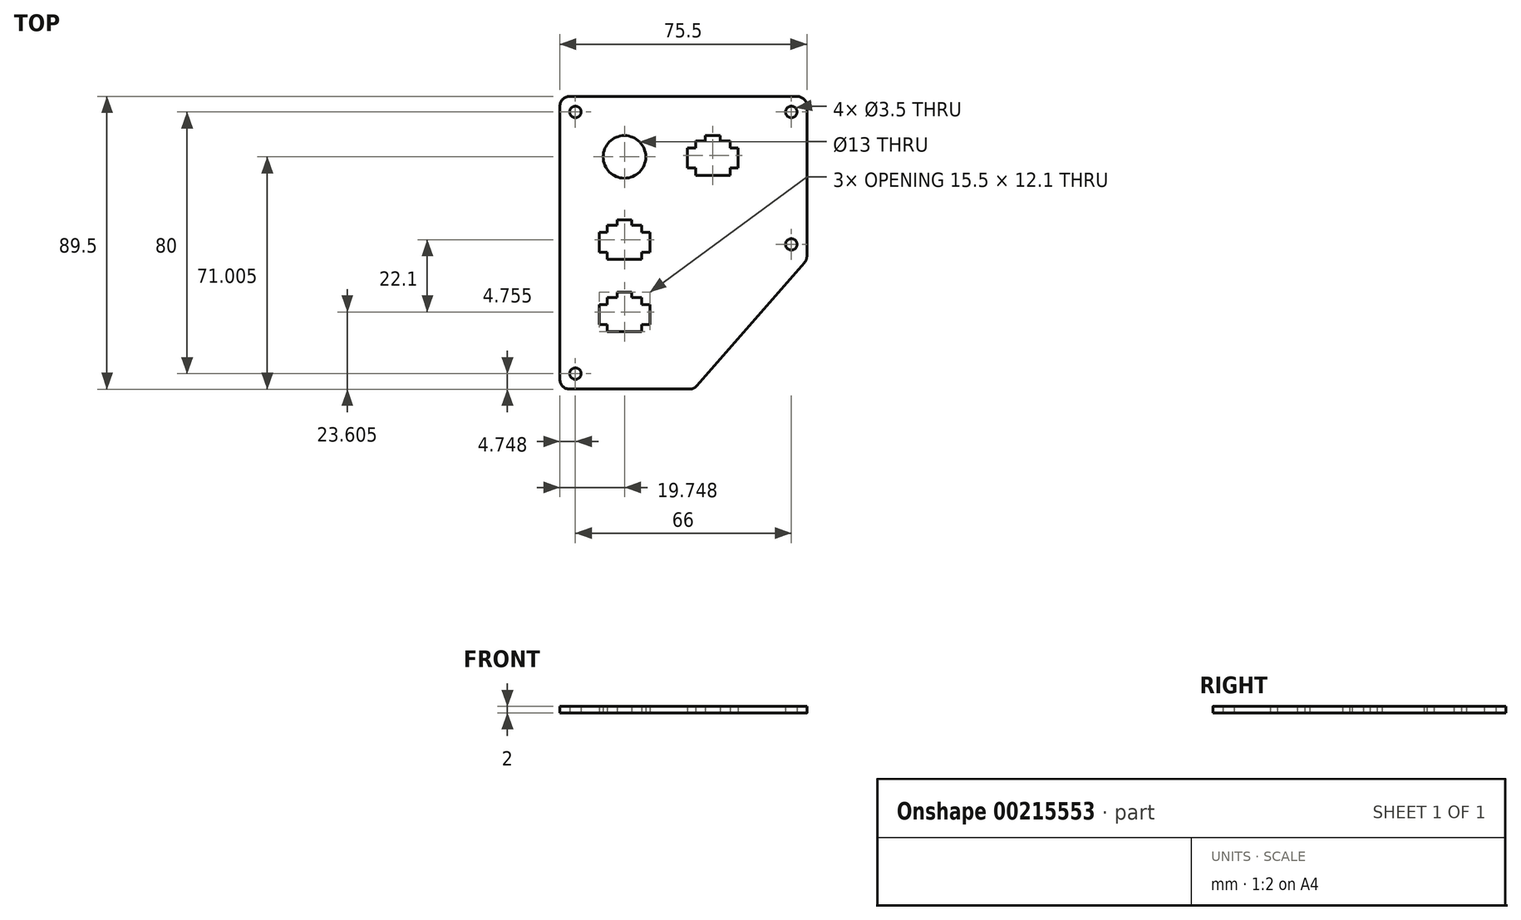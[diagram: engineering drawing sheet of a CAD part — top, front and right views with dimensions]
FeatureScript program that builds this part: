
annotation { "Feature Type Name" : "Feature", "Feature Type Description" : "" }
export const myFeature = defineFeature(function(context is Context, id is Id, definition is map)
    precondition{}
    {
        {
            var Q0;
            Q0=qCreatedBy(makeId("Top.planeOp"),FACE);
            var sketch = newSketch(context, id + "F0", { "sketchPlane" : qUnion([Q0])});
            skLineSegment(sketch, "E0", {"start": v(-37.21, 48.66) * mm, "end": v(38.29, 48.66) * mm});
            skLineSegment(sketch, "E1", {"start": v(38.29, 48.66) * mm, "end": v(38.29, -1.34) * mm});
            skLineSegment(sketch, "E2", {"start": v(38.29, -1.34) * mm, "end": v(3.79, -40.84) * mm});
            skLineSegment(sketch, "E3", {"start": v(3.79, -40.84) * mm, "end": v(-37.21, -40.84) * mm});
            skLineSegment(sketch, "E4", {"start": v(-37.21, -40.84) * mm, "end": v(-37.21, 48.66) * mm});
            skCircle(sketch, "E5", {"center": v(-32.46, 43.91) * mm, "radius": 1.75 * mm});
            skCircle(sketch, "E6", {"center": v(33.54, 43.91) * mm, "radius": 1.75 * mm});
            skCircle(sketch, "E7", {"center": v(33.54, 3.41) * mm, "radius": 1.75 * mm});
            skCircle(sketch, "E8", {"center": v(-32.46, -36.09) * mm, "radius": 1.75 * mm});
            skLineSegment(sketch, "E9", {"start": v(-25.21, 36.66) * mm, "end": v(26.29, 36.66) * mm, "construction": true});
            skLineSegment(sketch, "E10", {"start": v(26.29, 36.66) * mm, "end": v(26.29, -2.68) * mm, "construction": true});
            skLineSegment(sketch, "E11", {"start": v(26.29, -2.68) * mm, "end": v(2.25, -28.84) * mm, "construction": true});
            skLineSegment(sketch, "E12", {"start": v(2.25, -28.84) * mm, "end": v(-25.21, -28.84) * mm, "construction": true});
            skLineSegment(sketch, "E13", {"start": v(-25.21, -28.84) * mm, "end": v(-25.21, 36.66) * mm, "construction": true});
            skSolve(sketch);
        }
        {
            var Q0;
            Q0=qCreatedBy(makeId("Top.planeOp"),FACE);
            var sketch = newSketch(context, id + "F1", { "sketchPlane" : qUnion([Q0])});
            skLineSegment(sketch, "E14.bottom", {"start": v(-12.21, 9.31) * mm, "end": v(-22.71, 9.31) * mm});
            skLineSegment(sketch, "E14.top", {"start": v(-12.21, -1.19) * mm, "end": v(-22.71, -1.19) * mm});
            skLineSegment(sketch, "E14.left", {"start": v(-12.21, 9.31) * mm, "end": v(-12.21, -1.19) * mm});
            skLineSegment(sketch, "E14.right", {"start": v(-22.71, 9.31) * mm, "end": v(-22.71, -1.19) * mm});
            skPoint(sketch, "E14.middle", {"position": v(-17.46, 4.06) * mm});
            skLineSegment(sketch, "E15.bottom", {"start": v(-12.21, 7.11) * mm, "end": v(-9.71, 7.11) * mm});
            skLineSegment(sketch, "E15.top", {"start": v(-12.21, 1.01) * mm, "end": v(-9.71, 1.01) * mm});
            skLineSegment(sketch, "E15.left", {"start": v(-12.21, 7.11) * mm, "end": v(-12.21, 1.01) * mm});
            skLineSegment(sketch, "E15.right", {"start": v(-9.71, 7.11) * mm, "end": v(-9.71, 1.01) * mm});
            skPoint(sketch, "E15.middle", {"position": v(-10.96, 4.06) * mm});
            skLineSegment(sketch, "E16.bottom", {"start": v(-22.71, 7.11) * mm, "end": v(-25.21, 7.11) * mm});
            skLineSegment(sketch, "E16.top", {"start": v(-22.71, 1.01) * mm, "end": v(-25.21, 1.01) * mm});
            skLineSegment(sketch, "E16.left", {"start": v(-22.71, 7.11) * mm, "end": v(-22.71, 1.01) * mm});
            skLineSegment(sketch, "E16.right", {"start": v(-25.21, 7.11) * mm, "end": v(-25.21, 1.01) * mm});
            skPoint(sketch, "E16.middle", {"position": v(-23.96, 4.06) * mm});
            skLineSegment(sketch, "E17.bottom", {"start": v(-15.21, 9.31) * mm, "end": v(-19.71, 9.31) * mm});
            skLineSegment(sketch, "E17.top", {"start": v(-15.21, 10.91) * mm, "end": v(-19.71, 10.91) * mm});
            skLineSegment(sketch, "E17.left", {"start": v(-15.21, 9.31) * mm, "end": v(-15.21, 10.91) * mm});
            skLineSegment(sketch, "E17.right", {"start": v(-19.71, 9.31) * mm, "end": v(-19.71, 10.91) * mm});
            skPoint(sketch, "E17.middle", {"position": v(-17.46, 10.11) * mm});
            skLineSegment(sketch, "E18.bottom", {"start": v(14.79, 35.06) * mm, "end": v(4.29, 35.06) * mm});
            skLineSegment(sketch, "E18.top", {"start": v(14.79, 24.56) * mm, "end": v(4.29, 24.56) * mm});
            skLineSegment(sketch, "E18.left", {"start": v(14.79, 35.06) * mm, "end": v(14.79, 24.56) * mm});
            skLineSegment(sketch, "E18.right", {"start": v(4.29, 35.06) * mm, "end": v(4.29, 24.56) * mm});
            skPoint(sketch, "E18.middle", {"position": v(9.54, 29.81) * mm});
            skLineSegment(sketch, "E19.bottom", {"start": v(14.79, 32.86) * mm, "end": v(17.29, 32.86) * mm});
            skLineSegment(sketch, "E19.top", {"start": v(14.79, 26.76) * mm, "end": v(17.29, 26.76) * mm});
            skLineSegment(sketch, "E19.left", {"start": v(14.79, 32.86) * mm, "end": v(14.79, 26.76) * mm});
            skLineSegment(sketch, "E19.right", {"start": v(17.29, 32.86) * mm, "end": v(17.29, 26.76) * mm});
            skPoint(sketch, "E19.middle", {"position": v(16.04, 29.81) * mm});
            skLineSegment(sketch, "E20.bottom", {"start": v(4.29, 32.86) * mm, "end": v(1.79, 32.86) * mm});
            skLineSegment(sketch, "E20.top", {"start": v(4.29, 26.76) * mm, "end": v(1.79, 26.76) * mm});
            skLineSegment(sketch, "E20.left", {"start": v(4.29, 32.86) * mm, "end": v(4.29, 26.76) * mm});
            skLineSegment(sketch, "E20.right", {"start": v(1.79, 32.86) * mm, "end": v(1.79, 26.76) * mm});
            skPoint(sketch, "E20.middle", {"position": v(3.04, 29.81) * mm});
            skLineSegment(sketch, "E21.bottom", {"start": v(11.79, 35.06) * mm, "end": v(7.29, 35.06) * mm});
            skLineSegment(sketch, "E21.top", {"start": v(11.79, 36.66) * mm, "end": v(7.29, 36.66) * mm});
            skLineSegment(sketch, "E21.left", {"start": v(11.79, 35.06) * mm, "end": v(11.79, 36.66) * mm});
            skLineSegment(sketch, "E21.right", {"start": v(7.29, 35.06) * mm, "end": v(7.29, 36.66) * mm});
            skPoint(sketch, "E21.middle", {"position": v(9.54, 35.86) * mm});
            skLineSegment(sketch, "E22.bottom", {"start": v(-12.21, -12.79) * mm, "end": v(-22.71, -12.79) * mm});
            skLineSegment(sketch, "E22.top", {"start": v(-12.21, -23.29) * mm, "end": v(-22.71, -23.29) * mm});
            skLineSegment(sketch, "E22.left", {"start": v(-12.21, -12.79) * mm, "end": v(-12.21, -23.29) * mm});
            skLineSegment(sketch, "E22.right", {"start": v(-22.71, -12.79) * mm, "end": v(-22.71, -23.29) * mm});
            skPoint(sketch, "E22.middle", {"position": v(-17.46, -18.04) * mm});
            skLineSegment(sketch, "E23.bottom", {"start": v(-12.21, -14.99) * mm, "end": v(-9.71, -14.99) * mm});
            skLineSegment(sketch, "E23.top", {"start": v(-12.21, -21.09) * mm, "end": v(-9.71, -21.09) * mm});
            skLineSegment(sketch, "E23.left", {"start": v(-12.21, -14.99) * mm, "end": v(-12.21, -21.09) * mm});
            skLineSegment(sketch, "E23.right", {"start": v(-9.71, -14.99) * mm, "end": v(-9.71, -21.09) * mm});
            skPoint(sketch, "E23.middle", {"position": v(-10.96, -18.04) * mm});
            skLineSegment(sketch, "E24.bottom", {"start": v(-22.71, -14.99) * mm, "end": v(-25.21, -14.99) * mm});
            skLineSegment(sketch, "E24.top", {"start": v(-22.71, -21.09) * mm, "end": v(-25.21, -21.09) * mm});
            skLineSegment(sketch, "E24.left", {"start": v(-22.71, -14.99) * mm, "end": v(-22.71, -21.09) * mm});
            skLineSegment(sketch, "E24.right", {"start": v(-25.21, -14.99) * mm, "end": v(-25.21, -21.09) * mm});
            skPoint(sketch, "E24.middle", {"position": v(-23.96, -18.04) * mm});
            skLineSegment(sketch, "E25.bottom", {"start": v(-15.21, -12.79) * mm, "end": v(-19.71, -12.79) * mm});
            skLineSegment(sketch, "E25.top", {"start": v(-15.21, -11.19) * mm, "end": v(-19.71, -11.19) * mm});
            skLineSegment(sketch, "E25.left", {"start": v(-15.21, -12.79) * mm, "end": v(-15.21, -11.19) * mm});
            skLineSegment(sketch, "E25.right", {"start": v(-19.71, -12.79) * mm, "end": v(-19.71, -11.19) * mm});
            skPoint(sketch, "E25.middle", {"position": v(-17.46, -11.99) * mm});
            skCircle(sketch, "E26", {"center": v(-17.46, 30.16) * mm, "radius": 6.5 * mm});
            skCircle(sketch, "E27", {"center": v(-17.46, 30.16) * mm, "radius": 9.25 * mm, "construction": true});
            skSolve(sketch);
        }
        {
            var Q0;
            Q0 = qSketchRegion(id + "F0", true);
            extrude(context, id + "F2", {"entities" : qUnion([Q0]), "depth" : 2 * mm});
        }
        {
            var Q0;
            Q0 = qSketchRegion(id + "F1", true);
            extrude(context, id + "F3", {"entities" : qUnion([Q0]), "operationType" : NewBodyOperationType.REMOVE, "endBound" : BoundingType.THROUGH_ALL, "depth" : 25 * mm});
        }
        {
            var Q0;
            Q0=makeQuery(id+"F2.opExtrude","SWEPT_EDGE",EDGE,{"disambiguationData":[OSD([sQuery(id+"F0.wireOp",EDGE,"E0"),sQuery(id+"F0.wireOp",EDGE,"E4")])]});
            var Q1;
            Q1=makeQuery(id+"F2.opExtrude","SWEPT_EDGE",EDGE,{"disambiguationData":[OSD([sQuery(id+"F0.wireOp",EDGE,"E0"),sQuery(id+"F0.wireOp",EDGE,"E1")])]});
            var Q2;
            Q2=makeQuery(id+"F2.opExtrude","SWEPT_EDGE",EDGE,{"disambiguationData":[OSD([sQuery(id+"F0.wireOp",EDGE,"E1"),sQuery(id+"F0.wireOp",EDGE,"E2")])]});
            var Q3;
            Q3=makeQuery(id+"F2.opExtrude","SWEPT_EDGE",EDGE,{"disambiguationData":[OSD([sQuery(id+"F0.wireOp",EDGE,"E2"),sQuery(id+"F0.wireOp",EDGE,"E3")])]});
            var Q4;
            Q4=makeQuery(id+"F2.opExtrude","SWEPT_EDGE",EDGE,{"disambiguationData":[OSD([sQuery(id+"F0.wireOp",EDGE,"E3"),sQuery(id+"F0.wireOp",EDGE,"E4")])]});
            fillet(context, id + "F4", {"entities" : qUnion([Q0, Q1, Q2, Q3, Q4]), "radius" : 3 * mm, "tangentPropagation" : true, "allowEdgeOverflow" : false});
        }
    });
